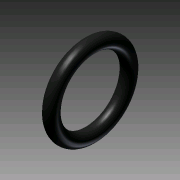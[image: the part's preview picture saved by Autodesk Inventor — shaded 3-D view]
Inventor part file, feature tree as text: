
AUTODESK INVENTOR PART (.ipt)
format: ipt  version: 2011 (Build 150239000, 239)  size: 98,304 bytes
history: native  units: in
note: dims shown in document units (in); Inventor stores cm internally (conversion verified against a paired STEP export)
features: revolve x1, sketch x1
ambient origin geometry x8: Origin, YZ Plane, XZ Plane, XY Plane, X Axis, Y Axis, Z Axis, Center Point
bodies: Solid1 (feature_tree)
feature tree (2):
  revolve  "Revolution1"  [1 undecoded]
  sketch  "Sketch1"  dims[d0=0.125in d1=0.3045in d2=90.0deg]
note: 1 required parameter value undecoded (feature->parameter linkage not recoverable at this tier; creation-order binding heuristic only, values carry confidence <= 0.55)
